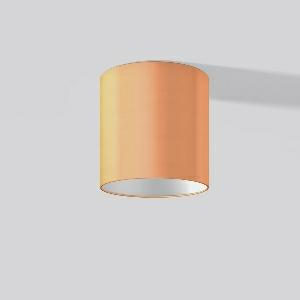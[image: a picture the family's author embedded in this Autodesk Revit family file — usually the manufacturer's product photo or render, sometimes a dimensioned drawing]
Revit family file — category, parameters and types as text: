
# Revit family: toledo_flatliner_901630_002_76_2e80
name_source: partatom
category: Lighting Fixtures
units: mm (PartAtom-declared; Revit-internal decimal feet)

## family parameters
Cut with Voids When Loaded = No
Host = Face
Light Source = No
Part Type = Normal
Room Calculation Point = No
Round Connector Dimension = Use Diameter
Shared = No

## types (1)
- 982300.002 (1 x LED Modul 830, 610 lm, 3000)
    Apparent Load = 8 VA
    CIE Flux Codes = 56 78 92 81 100
    Color Rendering = 80
    Color Temperature = 3000
    Default Elevation = 1800 mm
    Description = Series: TOLEDO FLATLINER
Decorative ceiling luminaire for interior decoration. Base luminaire prepared for the installation of fabric lampshade. Cylinder housing sheet steel, powder-coated. Housing: die cast aluminium and sheet steel, powder-coated. Bezel ring: die-cast aluminium, powder-coated. Lightguide and diffuser made of non-yellowing plastic (PMMA) opal matt. Modular design: With the basic luminaire, a square or cylindrical fabric lampshade must always be ordered separately. Fabric lampshades can be fitted to the basic luminaire without tools. Order satin finish diffuser as separate accessory. 
Colour: white
Diameter: 202 mm
Height: 65 mm
Lamp: LED
Socket: without socket
Colour temperature: 3000K
Colour rendering index (CRI): 80
System power: 7.7 W
Rated luminous flux: 610 lm
Luminous efficiency: 79 lm/W
Control gear: Converter, dimmable, DALI
Protection class: II
Type of protection: IP 40
    Height = 65 mm
    Lamp = 1 x LED Modul 830
    Lamp Light Flux = 610 lm
    Lamp count = 1
    Length = 202 mm
    Lifetime = 50000 h
    Luminous efficacy = 79 lm/W
    Manufacturer = RZB
    ModVariant = No
    Model = 901630.002.76
    Mounting Place = Ceiling
    Mounting Type = Surface mounted
    Number of Poles = 1
    OnlyDefault = Yes
    Power Factor = 1
    Product Name = TOLEDO FLATLINER
    Product group = Surface mounted ceiling Fabric lampshade luminaires
    ProductGroupID = 313
    Protection Class = Protection class II
    Protection Degree = IP 40
    RLX_Detail_Level = 1
    RLX_Emergency_Light_Flux = 0 lm
    RLX_Emergency_Type = 0
    RLX_Emergency_Type_DB = No
    RlxData = <blob elided: 62505 chars, md5=ff3b90c5>
    Socket = socket
    Standby Power = 0 W
    System Light Flux = 610 lm
    System Power = 8 W
    Type Image = toledo_flatliner_anbau_rund_orange_odeckel.jpg
    URL = http://relux.com
    VarID = 982300_002_5a54
    Voltage = 230 V
    Voltage Range = 220-240 V
    Weight = 0.00 kg
    Width = 0 mm  [stored 0 ft]

note: [stored X ft] marks values corroborated as IEEE doubles in the binary element streams (Revit-internal decimal feet)

## geometry (parser evidence)
native form markers: Blend x4, Sweep x13
no freeform markers — native parametric forms only
